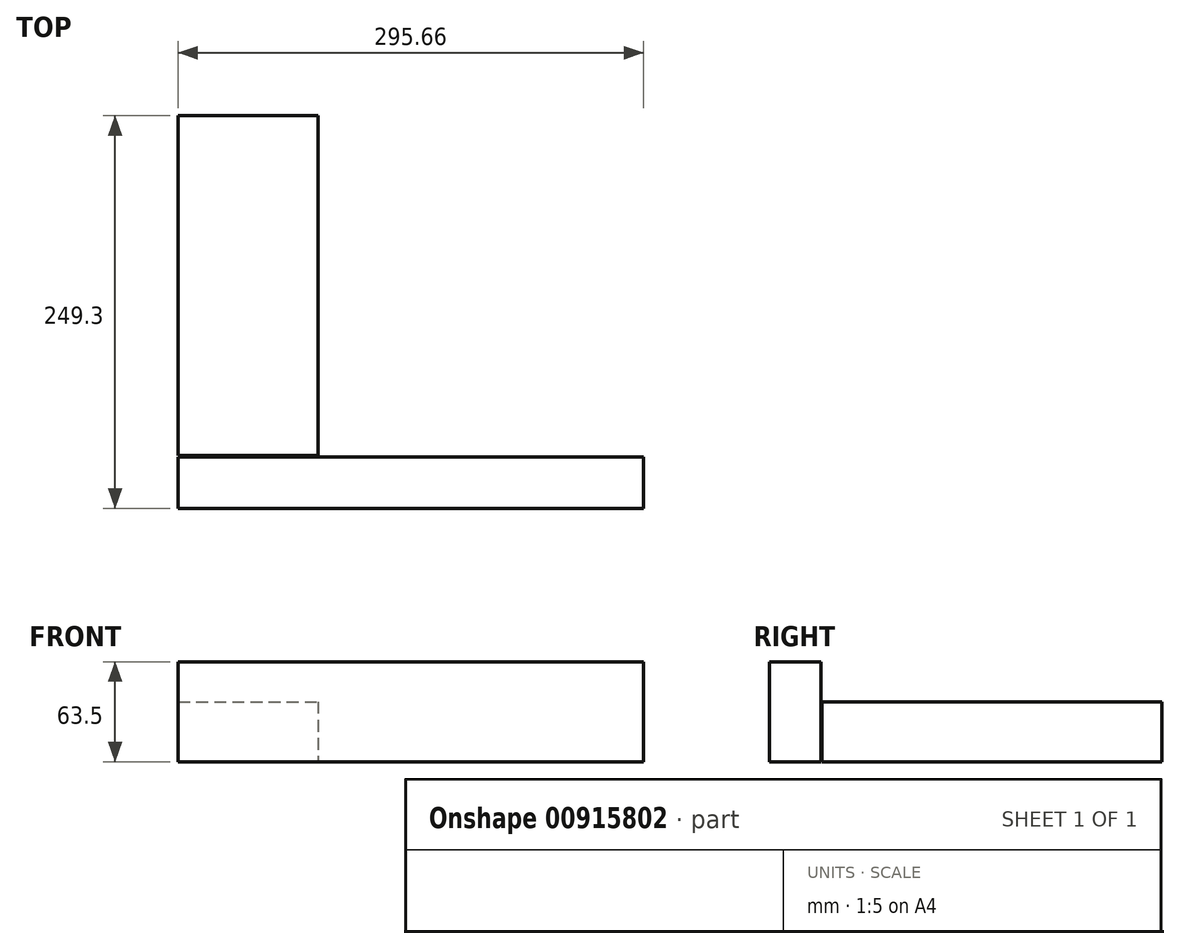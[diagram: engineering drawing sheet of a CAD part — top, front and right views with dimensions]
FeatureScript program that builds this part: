
annotation { "Feature Type Name" : "Feature", "Feature Type Description" : "" }
export const myFeature = defineFeature(function(context is Context, id is Id, definition is map)
    precondition{}
    {
        {
            var Q0;
            Q0=qCreatedBy(makeId("Top.planeOp"),FACE);
            var sketch = newSketch(context, id + "F0", { "sketchPlane" : qUnion([Q0])});
            skLineSegment(sketch, "E0.bottom", {"start": v(148.6, -125.41) * mm, "end": v(-148.6, -125.41) * mm, "construction": true});
            skLineSegment(sketch, "E0.top", {"start": v(148.6, 125.41) * mm, "end": v(-148.6, 125.41) * mm, "construction": true});
            skLineSegment(sketch, "E0.left", {"start": v(148.6, -125.41) * mm, "end": v(148.6, 125.41) * mm, "construction": true});
            skLineSegment(sketch, "E0.right", {"start": v(-148.6, -125.41) * mm, "end": v(-148.6, 125.41) * mm, "construction": true});
            skPoint(sketch, "E0.middle", {"position": v(0, 0) * mm});
            skLineSegment(sketch, "E1.bottom", {"start": v(145.41, -122.24) * mm, "end": v(-145.41, -122.24) * mm, "construction": true});
            skLineSegment(sketch, "E1.top", {"start": v(145.41, 122.24) * mm, "end": v(-145.41, 122.24) * mm, "construction": true});
            skLineSegment(sketch, "E1.left", {"start": v(145.42, -122.24) * mm, "end": v(145.42, 122.24) * mm, "construction": true});
            skLineSegment(sketch, "E1.right", {"start": v(-145.42, -122.24) * mm, "end": v(-145.42, 122.24) * mm, "construction": true});
            skSolve(sketch);
        }
        {
            var Q0;
            Q0=qCreatedBy(makeId("Top.planeOp"),FACE);
            var sketch = newSketch(context, id + "F1", { "sketchPlane" : qUnion([Q0])});
            skLineSegment(sketch, "E2.bottom", {"start": v(-147.83, 124.65) * mm, "end": v(-58.93, 124.65) * mm});
            skLineSegment(sketch, "E2.top", {"start": v(-147.83, -91.25) * mm, "end": v(-58.93, -91.25) * mm});
            skLineSegment(sketch, "E2.left", {"start": v(-147.83, 124.65) * mm, "end": v(-147.83, -91.25) * mm});
            skLineSegment(sketch, "E2.right", {"start": v(-58.93, 124.65) * mm, "end": v(-58.93, -91.25) * mm});
            skSolve(sketch);
        }
        {
            var Q0;
            Q0 = qSketchRegion(id + "F1", true);
            extrude(context, id + "F2", {"entities" : qUnion([Q0]), "depth" : 38.1 * mm, "offsetDistance" : 25.4 * mm});
        }
        {
            var Q0;
            Q0=qCreatedBy(makeId("Top.planeOp"),FACE);
            var sketch = newSketch(context, id + "F3", { "sketchPlane" : qUnion([Q0])});
            skLineSegment(sketch, "E3.bottom", {"start": v(-147.83, -124.65) * mm, "end": v(147.83, -124.65) * mm});
            skLineSegment(sketch, "E3.top", {"start": v(-147.83, -92.01) * mm, "end": v(147.83, -92.01) * mm});
            skLineSegment(sketch, "E3.left", {"start": v(-147.83, -124.65) * mm, "end": v(-147.83, -92.01) * mm});
            skLineSegment(sketch, "E3.right", {"start": v(147.83, -124.65) * mm, "end": v(147.83, -92.01) * mm});
            skSolve(sketch);
        }
        {
            var Q0;
            Q0 = qSketchRegion(id + "F3", true);
            extrude(context, id + "F4", {"entities" : qUnion([Q0]), "depth" : 63.5 * mm, "offsetDistance" : 25.4 * mm});
        }
    });
